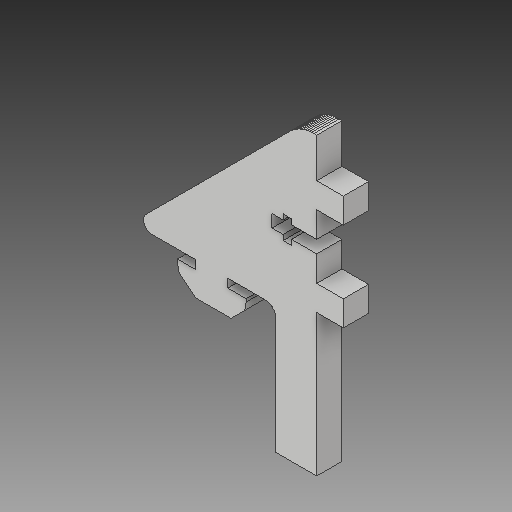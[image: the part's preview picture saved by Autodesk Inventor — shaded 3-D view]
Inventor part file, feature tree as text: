
AUTODESK INVENTOR PART (.ipt)
format: ipt  version: 2018 (Build 220112000, 112)  size: 363,008 bytes
history: native  units: mm
features: other x3, sketch x1
ambient origin geometry x8: Origin, YZ Plane, XZ Plane, XY Plane, X Axis, Y Axis, Z Axis, Center Point
bodies: Solid1 (feature_tree)
feature tree (4):
  other  "Y-Motor-Brace_MIR.ipt"
  other  "Solid1::Y-Motor-Brace_MIR.ipt"
  other  "TaggingFeature1"
  sketch  "Sketch1"  dims[d0=10.0mm]
